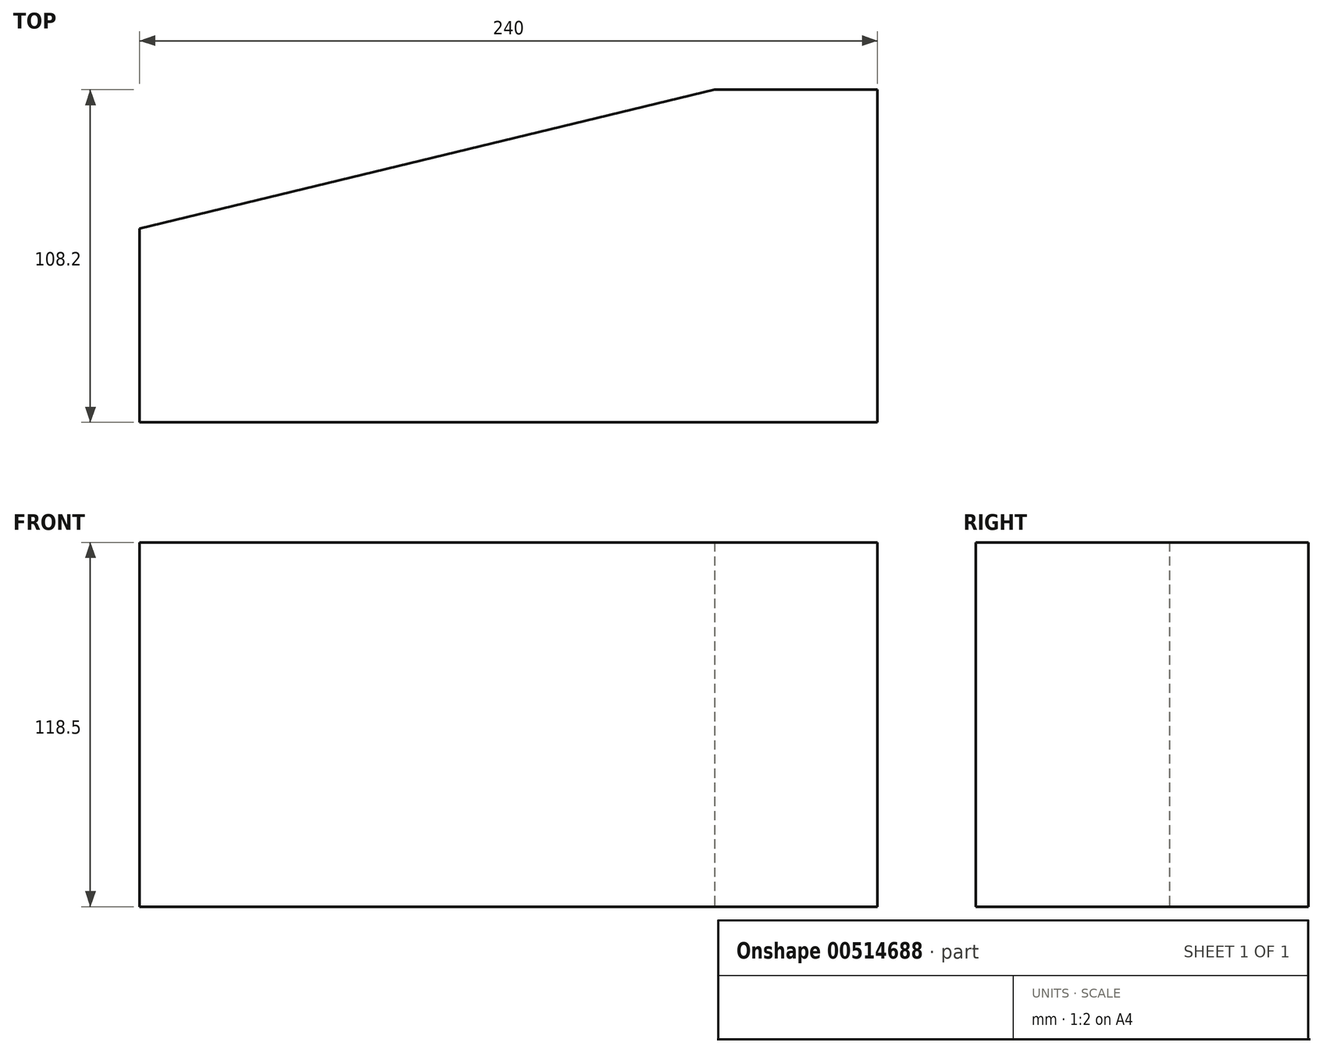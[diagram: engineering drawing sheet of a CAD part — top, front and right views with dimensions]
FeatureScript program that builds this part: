
annotation { "Feature Type Name" : "Feature", "Feature Type Description" : "" }
export const myFeature = defineFeature(function(context is Context, id is Id, definition is map)
    precondition{}
    {
        {
            var Q0;
            Q0=qCreatedBy(makeId("Top.planeOp"),FACE);
            var sketch = newSketch(context, id + "F0", { "sketchPlane" : qUnion([Q0])});
            skLineSegment(sketch, "E0", {"start": v(0, 0) * mm, "end": v(0, -108.2) * mm});
            skLineSegment(sketch, "E1", {"start": v(0, 0) * mm, "end": v(-53, 0) * mm});
            skLineSegment(sketch, "E2", {"start": v(0, -108.2) * mm, "end": v(-240, -108.2) * mm});
            skLineSegment(sketch, "E3", {"start": v(-240, -108.2) * mm, "end": v(-240, -45.2) * mm});
            skLineSegment(sketch, "E4", {"start": v(-240, -45.2) * mm, "end": v(-53, 0) * mm});
            skSolve(sketch);
        }
        {
            var Q0;
            Q0=makeQuery(id+"F0.imprint","IMPRINT",FACE,{"disambiguationData":[TD([[makeQuery(id+"F0.imprint","IMPRINT",EDGE,{"derivedFrom":sQuery(id+"F0.wireOp",EDGE,"E0")}),-1.0]])]});
            extrude(context, id + "F1", {"entities" : qUnion([Q0]), "depth" : 59.25 * mm, "offsetDistance" : 25 * mm, "hasSecondDirection" : true, "secondDirectionOppositeDirection" : true, "secondDirectionDepth" : 59.25 * mm});
        }
    });
